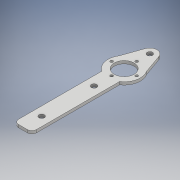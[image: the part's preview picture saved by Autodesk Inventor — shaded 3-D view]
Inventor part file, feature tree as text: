
AUTODESK INVENTOR PART (.ipt)
format: ipt  version: 2018.3 (Build 223284000, 284)  size: 135,168 bytes
history: native  units: mm
features: extrude x1, fillet x1, sketch x1
ambient origin geometry x8: Origin, YZ Plane, XZ Plane, XY Plane, X Axis, Y Axis, Z Axis, Center Point
bodies: Body1 (feature_tree)
feature tree (3):
  extrude  "Extrusion2"  Depth=5.0mm
  fillet  "Fillet1"  Radius=6.0mm
  sketch  "Sketch2"  dims[d5=8.0mm d13=6.0mm d19=4.0mm d20=4.0mm d25=4.0mm d26=4.0mm d30=35.9918mm d47=6.0mm d51=6.0mm d55=35.9918mm d56=22.098mm d58=3.1mm d59=40.0mm d61=360.0deg d63=6.0mm d64=13.9954mm d65=5.0mm d66=3.175mm d67=0.0mm d68=5.0mm]
